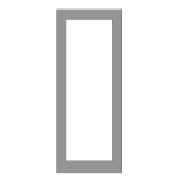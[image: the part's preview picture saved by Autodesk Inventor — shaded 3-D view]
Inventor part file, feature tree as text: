
AUTODESK INVENTOR PART (.ipt)
format: ipt  version: 2020 (Build 240168000, 168)  size: 192,512 bytes
history: native  units: in
note: dims shown in document units (in); Inventor stores cm internally (conversion verified against a paired STEP export)
features: sketch x5, other x4, plane x3, split x2, extrude x1, hole x1
ambient origin geometry x8: Origin, YZ Plane, XZ Plane, XY Plane, X Axis, Y Axis, Z Axis, Center Point
bodies: Solid1 (feature_tree), Body (feature_tree)
feature tree (16):
  other  "Driven Length"
  other  "Frame Generator"
  other  "Start Plane"
  other  "End Plane"
  plane  "Work Plane6"
  split  "Split1"
  plane  "Work Plane7"
  split  "Split2"
  extrude  "Extrusion3"  Depth=3.0in
  hole  "Hole1"  [1 undecoded]
  sketch  "Sketch"  dims[d8=0.13in d9=0.0in d14=90.0deg d11=30.0in d19=1.0in d20=0.0in d23=1.125in d26=0.5in d27=0.5in d28=0.7874in d30=28.0in d31=0.7874in d33=2.0in d36=0.196in d37=0.146in d38=0.385in d39=0.02in d40=0.5635in d41=1.0in d42=0.8108in d43=0.3135in d44=3.5in d45=0.3135in d46=3.5in d48=1.25in d49=2.0in d50=2.0in d51=1.25in d52=1.125in]
  sketch  "Sketch6"  dims[d0=1.0in d1=3.0in]
  plane  "Work Plane5"
  sketch  "Sketch7"  dims[d2=0.125in d3=0.125in]
  sketch  "Sketch8"  dims[d6=-0.5in]
  sketch  "Sketch9"  dims[d7=29.5in]
note: 1 required parameter value undecoded (feature->parameter linkage not recoverable at this tier; creation-order binding heuristic only, values carry confidence <= 0.55)
